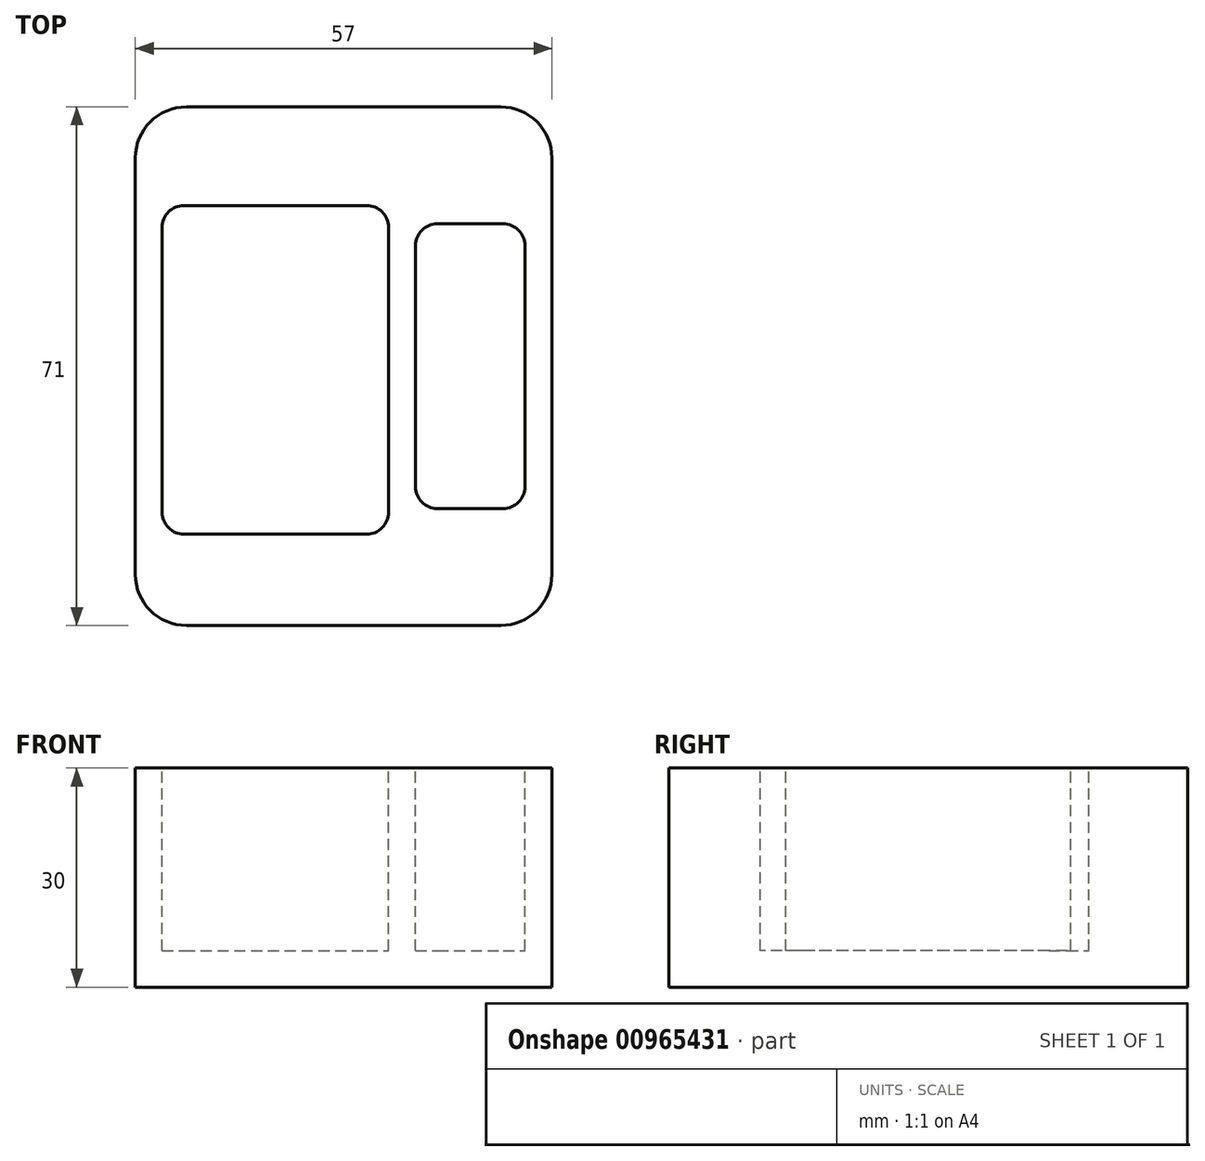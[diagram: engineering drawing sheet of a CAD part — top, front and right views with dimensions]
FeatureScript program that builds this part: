
annotation { "Feature Type Name" : "Feature", "Feature Type Description" : "" }
export const myFeature = defineFeature(function(context is Context, id is Id, definition is map)
    precondition{}
    {
        {
            var Q0;
            Q0=qCreatedBy(makeId("Top.planeOp"),FACE);
            var sketch = newSketch(context, id + "F0", { "sketchPlane" : qUnion([Q0])});
            skLineSegment(sketch, "E0.bottom", {"start": v(28.5, -35.5) * mm, "end": v(-28.5, -35.5) * mm});
            skLineSegment(sketch, "E0.top", {"start": v(28.5, 35.5) * mm, "end": v(-28.5, 35.5) * mm});
            skLineSegment(sketch, "E0.left", {"start": v(28.5, -35.5) * mm, "end": v(28.5, 35.5) * mm});
            skLineSegment(sketch, "E0.right", {"start": v(-28.5, -35.5) * mm, "end": v(-28.5, 35.5) * mm});
            skPoint(sketch, "E0.middle", {"position": v(0, 0) * mm});
            skSolve(sketch);
        }
        {
            var Q0;
            Q0 = qSketchRegion(id + "F0", true);
            extrude(context, id + "F1", {"entities" : qUnion([Q0]), "depth" : 30 * mm, "offsetDistance" : 25 * mm});
        }
        {
            var Q0;
            Q0=makeQuery(id+"F1.opExtrude","CAP_FACE",FACE,{"disambiguationData":[OSD([sQuery(id+"F0.wireOp",EDGE,"E0.bottom"),sQuery(id+"F0.wireOp",EDGE,"E0.top"),sQuery(id+"F0.wireOp",EDGE,"E0.left"),sQuery(id+"F0.wireOp",EDGE,"E0.right")])],"isStart":false});
            var sketch = newSketch(context, id + "F2", { "sketchPlane" : qUnion([Q0])});
            skLineSegment(sketch, "E1.bottom", {"start": v(9.83, 19.5) * mm, "end": v(24.83, 19.5) * mm});
            skLineSegment(sketch, "E1.top", {"start": v(9.83, -19.5) * mm, "end": v(24.83, -19.5) * mm});
            skLineSegment(sketch, "E1.left", {"start": v(9.83, 19.5) * mm, "end": v(9.83, -19.5) * mm});
            skLineSegment(sketch, "E1.right", {"start": v(24.83, 19.5) * mm, "end": v(24.83, -19.5) * mm});
            skLineSegment(sketch, "E2.bottom", {"start": v(-24.84, 22) * mm, "end": v(6.16, 22) * mm});
            skLineSegment(sketch, "E2.top", {"start": v(-24.84, -23) * mm, "end": v(6.16, -23) * mm});
            skLineSegment(sketch, "E2.left", {"start": v(-24.84, 22) * mm, "end": v(-24.84, -23) * mm});
            skLineSegment(sketch, "E2.right", {"start": v(6.16, 22) * mm, "end": v(6.16, -23) * mm});
            skSolve(sketch);
        }
        {
            var Q0;
            Q0=makeQuery(id+"F2.imprint","IMPRINT",FACE,{"disambiguationData":[TD([[makeQuery(id+"F2.imprint","IMPRINT",EDGE,{"derivedFrom":sQuery(id+"F2.wireOp",EDGE,"E2.bottom")}),-1.0]])]});
            var Q1;
            Q1=makeQuery(id+"F2.imprint","IMPRINT",FACE,{"disambiguationData":[TD([[makeQuery(id+"F2.imprint","IMPRINT",EDGE,{"derivedFrom":sQuery(id+"F2.wireOp",EDGE,"E1.bottom")}),-1.0]])]});
            extrude(context, id + "F3", {"entities" : qUnion([Q0, Q1]), "operationType" : NewBodyOperationType.REMOVE, "oppositeDirection" : true, "depth" : 25 * mm, "offsetDistance" : 25 * mm});
        }
        {
            var Q0;
            Q0=makeQuery(id+"F1.opExtrude","SWEPT_EDGE",EDGE,{"disambiguationData":[OSD([sQuery(id+"F0.wireOp",EDGE,"E0.top"),sQuery(id+"F0.wireOp",EDGE,"E0.left")])]});
            var Q1;
            Q1=makeQuery(id+"F1.opExtrude","SWEPT_EDGE",EDGE,{"disambiguationData":[OSD([sQuery(id+"F0.wireOp",EDGE,"E0.bottom"),sQuery(id+"F0.wireOp",EDGE,"E0.left")])]});
            var Q2;
            Q2=makeQuery(id+"F1.opExtrude","SWEPT_EDGE",EDGE,{"disambiguationData":[OSD([sQuery(id+"F0.wireOp",EDGE,"E0.bottom"),sQuery(id+"F0.wireOp",EDGE,"E0.right")])]});
            var Q3;
            Q3=makeQuery(id+"F1.opExtrude","SWEPT_EDGE",EDGE,{"disambiguationData":[OSD([sQuery(id+"F0.wireOp",EDGE,"E0.top"),sQuery(id+"F0.wireOp",EDGE,"E0.right")])]});
            fillet(context, id + "F4", {"entities" : qUnion([Q0, Q1, Q2, Q3]), "radius" : 7 * mm, "tangentPropagation" : true, "allowEdgeOverflow" : false});
        }
        {
            var Q0;
            Q0=makeQuery(id+"F3.boolean.opBoolean","COPY",EDGE,{"derivedFrom":makeQuery(id+"F3.opExtrude","SWEPT_EDGE",EDGE,{"disambiguationData":[OSD([sQuery(id+"F2.wireOp",EDGE,"E1.bottom"),sQuery(id+"F2.wireOp",EDGE,"E1.right")])]})});
            var Q1;
            Q1=makeQuery(id+"F3.boolean.opBoolean","COPY",EDGE,{"derivedFrom":makeQuery(id+"F3.opExtrude","SWEPT_EDGE",EDGE,{"disambiguationData":[OSD([sQuery(id+"F2.wireOp",EDGE,"E1.top"),sQuery(id+"F2.wireOp",EDGE,"E1.right")])]})});
            var Q2;
            Q2=makeQuery(id+"F3.boolean.opBoolean","COPY",EDGE,{"derivedFrom":makeQuery(id+"F3.opExtrude","SWEPT_EDGE",EDGE,{"disambiguationData":[OSD([sQuery(id+"F2.wireOp",EDGE,"E2.top"),sQuery(id+"F2.wireOp",EDGE,"E2.right")])]})});
            var Q3;
            Q3=makeQuery(id+"F3.boolean.opBoolean","COPY",EDGE,{"derivedFrom":makeQuery(id+"F3.opExtrude","SWEPT_EDGE",EDGE,{"disambiguationData":[OSD([sQuery(id+"F2.wireOp",EDGE,"E2.bottom"),sQuery(id+"F2.wireOp",EDGE,"E2.right")])]})});
            var Q4;
            Q4=makeQuery(id+"F3.boolean.opBoolean","COPY",EDGE,{"derivedFrom":makeQuery(id+"F3.opExtrude","SWEPT_EDGE",EDGE,{"disambiguationData":[OSD([sQuery(id+"F2.wireOp",EDGE,"E2.bottom"),sQuery(id+"F2.wireOp",EDGE,"E2.left")])]})});
            var Q5;
            Q5=makeQuery(id+"F3.boolean.opBoolean","COPY",EDGE,{"derivedFrom":makeQuery(id+"F3.opExtrude","SWEPT_EDGE",EDGE,{"disambiguationData":[OSD([sQuery(id+"F2.wireOp",EDGE,"E1.bottom"),sQuery(id+"F2.wireOp",EDGE,"E1.left")])]})});
            var Q6;
            Q6=makeQuery(id+"F3.boolean.opBoolean","COPY",EDGE,{"derivedFrom":makeQuery(id+"F3.opExtrude","SWEPT_EDGE",EDGE,{"disambiguationData":[OSD([sQuery(id+"F2.wireOp",EDGE,"E2.top"),sQuery(id+"F2.wireOp",EDGE,"E2.left")])]})});
            var Q7;
            Q7=makeQuery(id+"F3.boolean.opBoolean","COPY",EDGE,{"derivedFrom":makeQuery(id+"F3.opExtrude","SWEPT_EDGE",EDGE,{"disambiguationData":[OSD([sQuery(id+"F2.wireOp",EDGE,"E1.top"),sQuery(id+"F2.wireOp",EDGE,"E1.left")])]})});
            fillet(context, id + "F5", {"entities" : qUnion([Q0, Q1, Q2, Q3, Q4, Q5, Q6, Q7]), "radius" : 3 * mm, "tangentPropagation" : true, "allowEdgeOverflow" : false});
        }
    });
